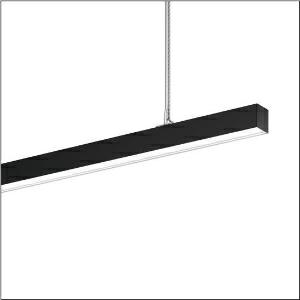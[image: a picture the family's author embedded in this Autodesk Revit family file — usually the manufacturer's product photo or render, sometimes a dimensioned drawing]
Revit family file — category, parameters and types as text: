
# Revit family: silica_21_51mx30dc49bb
name_source: partatom
category: Lighting Fixtures
units: mm (PartAtom-declared; Revit-internal decimal feet)

## family parameters
Cut with Voids When Loaded = No
Host = Face
Light Source = No
Part Type = Normal
Room Calculation Point = No
Round Connector Dimension = Use Diameter
Shared = No

## types (1)
- --- (1 x LED, 10520 lm, 64.1 W, 4000K)
    Apparent Load = 64 VA
    CIE Flux Codes = 47 79 96 57 100
    Color Rendering = 80
    Color Temperature = 4000K
    Default Elevation = 1800 mm
    Description = Silica 21, office luminaire, primary optical cover: cover, of PMMA, opal, light emission: direct/indirect distribution, primary light characteristic: symmetric, installation type: suspended mounting, LED, rated luminous flux: 10.520lm, luminous efficacy: 164lm/W, light colour: 840, colour temperature: 4000K, control gear: DALI 2, with terminal, 3+2-pole, max. 2.5mm², mains connection: 220..240V, AC, 50/60Hz, rated input power: 64.1W, luminaire housing, of aluminium, matt jet black (RAL 9005), length: 3.004mm, width: 53mm, height: 53mm, protection rating (complete): IP20, insulation class (complete): insulation class I (protective earthing), certification: CE, permissible operating ambient temperature: 0..+35°C, standard: EN 50419, packaging unit: 1 piece
    Height = 53 mm
    Lamp = 1 x LED
    Lamp Light Flux = 10520 lm
    Lamp Power = 64.1 W
    Lamp count = 1
    Length = 3004 mm
    Luminous efficacy = 164 lm/W
    Manufacturer = Siteco
    ModVariant = No
    Model = 51MX30DC49BB
    Mounting Place = Ceiling
    Mounting Type = Pendant
    Number of Poles = 1
    OnlyDefault = Yes
    Power Factor = 1
    Product Name = Silica 21
    Product group = office luminaire | ceiling pendant
    ProductGroupID = 903
    Protection Class = Protection class I
    Protection Degree = IP 20
    RLX_Detail_Level = 1
    RLX_Emergency_Light_Flux = 0 lm
    RLX_Emergency_Type = 0
    RLX_Emergency_Type_DB = No
    RlxData = <blob elided: 26085 chars, md5=4138e6a3>
    Socket = socket
    Standby Power = 0 W
    System Light Flux = 10520 lm
    System Power = 64 W
    Type Comments = factory setting: luminous flux: 100 % | dim-lin: 254 | 218 mA
    Type Image = l_1335856.jpg
    URL = http://relux.com
    VarID = @adj_118991
    Voltage = 0 V
    Weight = 0.00 kg
    Width = 53 mm

## geometry (parser evidence)
native form markers: Blend x4, Sweep x15
no freeform markers — native parametric forms only
